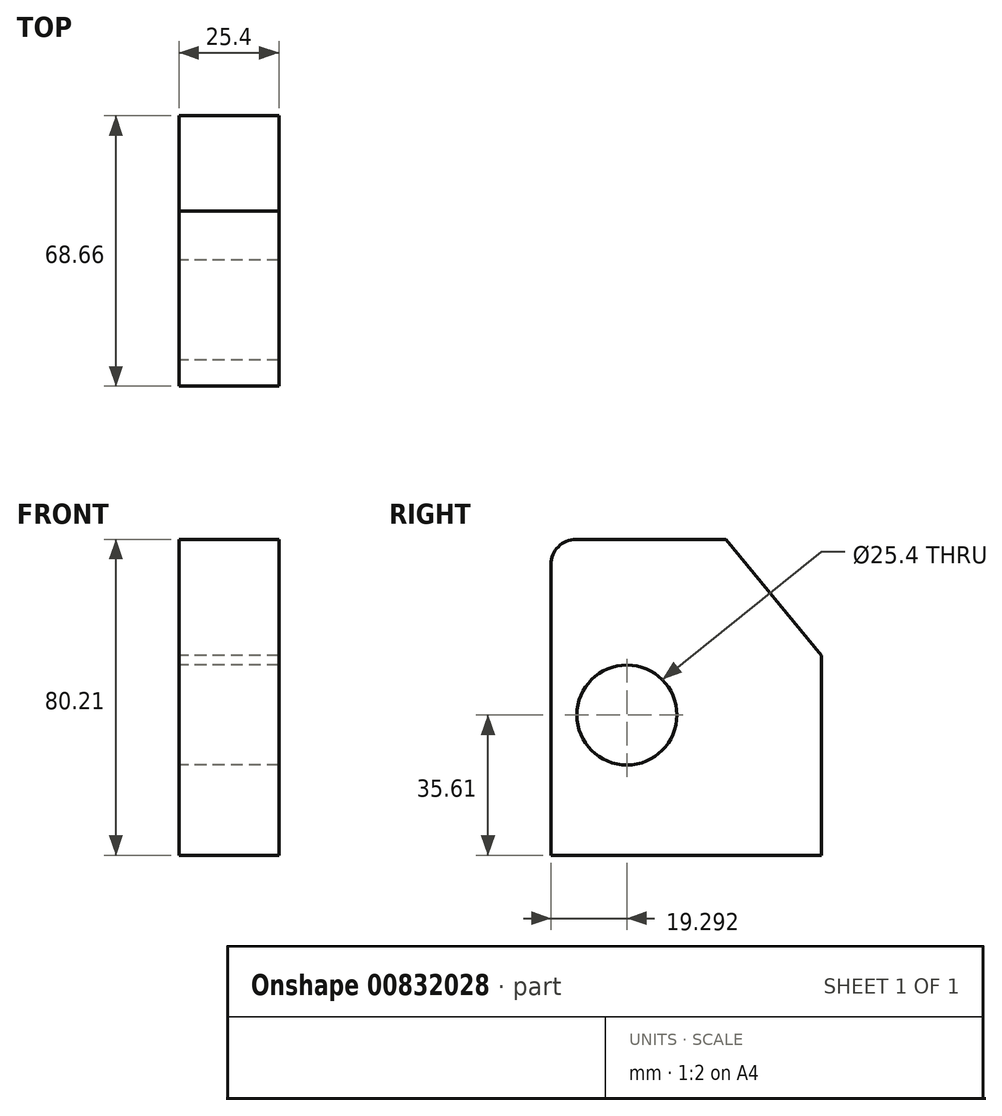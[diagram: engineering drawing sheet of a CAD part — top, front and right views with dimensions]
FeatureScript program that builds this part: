
annotation { "Feature Type Name" : "Feature", "Feature Type Description" : "" }
export const myFeature = defineFeature(function(context is Context, id is Id, definition is map)
    precondition{}
    {
        {
            var Q0;
            Q0=qCreatedBy(makeId("Right.planeOp"),FACE);
            var sketch = newSketch(context, id + "F0", { "sketchPlane" : qUnion([Q0])});
            skLineSegment(sketch, "E0.bottom", {"start": v(-46.55, 44.6) * mm, "end": v(-8.45, 44.6) * mm});
            skLineSegment(sketch, "E0.top", {"start": v(-52.9, -35.61) * mm, "end": v(15.76, -35.61) * mm});
            skLineSegment(sketch, "E0.left", {"start": v(-52.9, 38.25) * mm, "end": v(-52.9, -35.61) * mm});
            skLineSegment(sketch, "E0.right", {"start": v(15.76, 15.19) * mm, "end": v(15.76, -35.61) * mm});
            skPoint(sketch, "E1.visualSharp", {"position": v(-52.9, 44.6) * mm});
            skArc(sketch, "E1.filletArc", {"start": v(-46.55, 44.6) * mm, "mid": v(-51.04, 42.74) * mm, "end": v(-52.9, 38.25) * mm});
            skLineSegment(sketch, "E2", {"start": v(-8.45, 44.6) * mm, "end": v(15.76, 15.19) * mm});
            skCircle(sketch, "E3", {"center": v(-33.6, 0) * mm, "radius": 12.7 * mm});
            skSolve(sketch);
        }
        {
            var Q0;
            Q0 = qSketchRegion(id + "F0", true);
            extrude(context, id + "F1", {"entities" : qUnion([Q0]), "depth" : 25.4 * mm, "offsetDistance" : 25.4 * mm});
        }
    });
